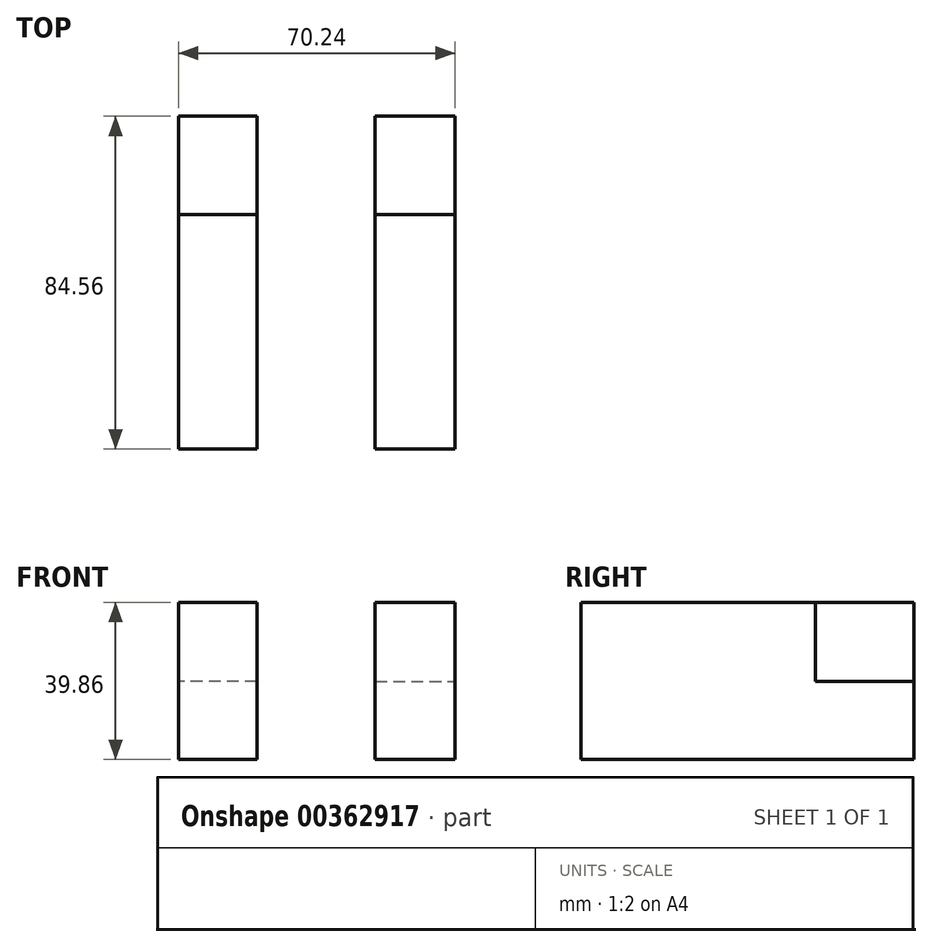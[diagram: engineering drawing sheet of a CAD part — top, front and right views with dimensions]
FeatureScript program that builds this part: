
annotation { "Feature Type Name" : "Feature", "Feature Type Description" : "" }
export const myFeature = defineFeature(function(context is Context, id is Id, definition is map)
    precondition{}
    {
        {
            var Q0;
            Q0=qCreatedBy(makeId("Front.planeOp"),FACE);
            var sketch = newSketch(context, id + "F0", { "sketchPlane" : qUnion([Q0])});
            skLineSegment(sketch, "E0.bottom", {"start": v(-110, -30) * mm, "end": v(110, -30) * mm});
            skLineSegment(sketch, "E0.top", {"start": v(-110, 30) * mm, "end": v(110, 30) * mm});
            skLineSegment(sketch, "E0.left", {"start": v(-110, -30) * mm, "end": v(-110, 30) * mm});
            skLineSegment(sketch, "E0.right", {"start": v(110, -30) * mm, "end": v(110, 30) * mm});
            skPoint(sketch, "E0.middle", {"position": v(0, 0) * mm});
            skLineSegment(sketch, "E1", {"start": v(-110, 0) * mm, "end": v(110, 0) * mm});
            skSolve(sketch);
        }
        {
            var Q0;
            {var subQ0=sQuery(id+"F0.wireOp",EDGE,"E0.top");Q0=makeQuery(id+"F0.imprint","IMPRINT",FACE,{"disambiguationData":[TD([[makeQuery(id+"F0.imprint","IMPRINT",EDGE,{"derivedFrom":subQ0}),-1.0]])]});}
            var sketch = newSketch(context, id + "F1", { "sketchPlane" : qUnion([Q0])});
            skLineSegment(sketch, "E2.bottom", {"start": v(-15.15, 0) * mm, "end": v(-35.07, 0) * mm});
            skLineSegment(sketch, "E2.top", {"start": v(-15.15, 20.04) * mm, "end": v(-35.07, 20.04) * mm});
            skLineSegment(sketch, "E2.left", {"start": v(-15.15, 0) * mm, "end": v(-15.15, 20.04) * mm});
            skLineSegment(sketch, "E2.right", {"start": v(-35.07, 0) * mm, "end": v(-35.07, 20.04) * mm});
            skLineSegment(sketch, "E3.bottom", {"start": v(14.9, 20.04) * mm, "end": v(35.17, 20.04) * mm});
            skLineSegment(sketch, "E3.top", {"start": v(14.9, 0) * mm, "end": v(35.17, 0) * mm});
            skLineSegment(sketch, "E3.left", {"start": v(14.9, 20.04) * mm, "end": v(14.9, 0) * mm});
            skLineSegment(sketch, "E3.right", {"start": v(35.17, 20.04) * mm, "end": v(35.17, 0) * mm});
            skLineSegment(sketch, "E4.top", {"start": v(-15.15, -19.82) * mm, "end": v(-35.07, -19.82) * mm});
            skLineSegment(sketch, "E4.left", {"start": v(-15.15, 0) * mm, "end": v(-15.15, -19.82) * mm});
            skLineSegment(sketch, "E4.right", {"start": v(-35.07, 0) * mm, "end": v(-35.07, -19.82) * mm});
            skLineSegment(sketch, "E5.top", {"start": v(14.9, -19.82) * mm, "end": v(35.17, -19.82) * mm});
            skLineSegment(sketch, "E5.left", {"start": v(14.9, 0) * mm, "end": v(14.9, -19.82) * mm});
            skLineSegment(sketch, "E5.right", {"start": v(35.17, 0) * mm, "end": v(35.17, -19.82) * mm});
            skSolve(sketch);
        }
        {
            var Q0;
            {var subQ0=sQuery(id+"F0.wireOp",EDGE,"E0.bottom");Q0=makeQuery(id+"F0.imprint","IMPRINT",FACE,{"disambiguationData":[TD([[makeQuery(id+"F0.imprint","IMPRINT",EDGE,{"derivedFrom":subQ0}),1.0]])]});}
            var sketch = newSketch(context, id + "F2", { "sketchPlane" : qUnion([Q0])});
            skLineSegment(sketch, "E6.bottom", {"start": v(-15.22, 0) * mm, "end": v(14.78, 0) * mm});
            skLineSegment(sketch, "E6.left", {"start": v(-15.22, 0) * mm, "end": v(-15.22, 19.99) * mm});
            skLineSegment(sketch, "E6.right", {"start": v(14.78, 0) * mm, "end": v(14.78, 19.99) * mm});
            skSolve(sketch);
        }
        {
            var Q0;
            Q0=makeQuery(id+"F1.imprint","IMPRINT",FACE,{"disambiguationData":[TD([[makeQuery(id+"F1.imprint","IMPRINT",EDGE,{"derivedFrom":sQuery(id+"F1.wireOp",EDGE,"E2.top")}),1.0]])]});
            var Q1;
            Q1=makeQuery(id+"F1.imprint","IMPRINT",FACE,{"disambiguationData":[TD([[makeQuery(id+"F1.imprint","IMPRINT",EDGE,{"derivedFrom":sQuery(id+"F1.wireOp",EDGE,"E3.bottom")}),-1.0]])]});
            extrude(context, id + "F3", {"entities" : qUnion([Q0, Q1]), "depth" : 25 * mm});
        }
        {
            var Q0;
            Q0 = qSketchRegion(id + "F2", true);
            var Q1;
            Q1 = qSketchRegion(id + "F1", true);
            extrude(context, id + "F4", {"entities" : qUnion([Q0, Q1]), "endBound" : BoundingType.THROUGH_ALL, "depth" : 46.7 * mm});
        }
        {
            var Q0;
            Q0=makeQuery(id+"F3.opExtrude","SWEPT_FACE",FACE,{"disambiguationData":[OSD([sQuery(id+"F1.wireOp",EDGE,"E2.right")])]});
            extrude(context, id + "F5", {"entities" : qUnion([Q0]), "operationType" : NewBodyOperationType.REMOVE, "oppositeDirection" : true, "depth" : 20.1 * mm});
        }
    });
